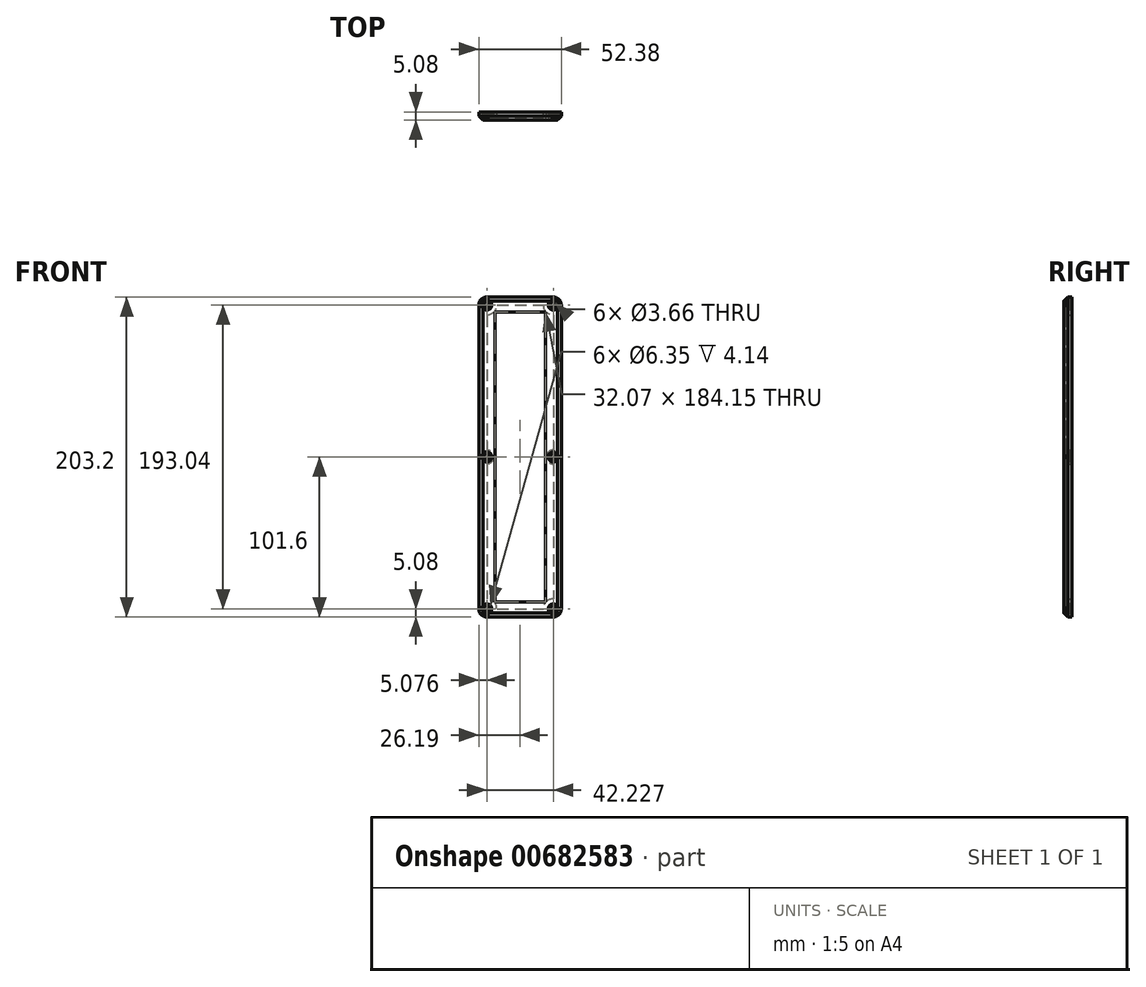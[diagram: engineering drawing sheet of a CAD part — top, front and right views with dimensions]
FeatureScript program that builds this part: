
annotation { "Feature Type Name" : "Feature", "Feature Type Description" : "" }
export const myFeature = defineFeature(function(context is Context, id is Id, definition is map)
    precondition{}
    {
        {
            var Q0;
            Q0=qCreatedBy(makeId("Front.planeOp"),FACE);
            var sketch = newSketch(context, id + "F0", { "sketchPlane" : qUnion([Q0])});
            skLineSegment(sketch, "E0.bottom", {"start": v(21.11, 101.6) * mm, "end": v(-21.11, 101.6) * mm});
            skLineSegment(sketch, "E0.top", {"start": v(21.11, -101.6) * mm, "end": v(-21.11, -101.6) * mm});
            skLineSegment(sketch, "E0.left", {"start": v(26.2, 96.52) * mm, "end": v(26.2, -96.52) * mm});
            skLineSegment(sketch, "E0.right", {"start": v(-26.2, 96.52) * mm, "end": v(-26.2, -96.52) * mm});
            skPoint(sketch, "E0.middle", {"position": v(0, 0) * mm});
            skPoint(sketch, "E1.visualSharp", {"position": v(-26.2, 101.6) * mm});
            skArc(sketch, "E1.filletArc", {"start": v(-21.11, 101.6) * mm, "mid": v(-24.7, 100.11) * mm, "end": v(-26.2, 96.52) * mm});
            skPoint(sketch, "E2.visualSharp", {"position": v(26.2, 101.6) * mm});
            skArc(sketch, "E2.filletArc", {"start": v(26.2, 96.52) * mm, "mid": v(24.7, 100.11) * mm, "end": v(21.11, 101.6) * mm});
            skPoint(sketch, "E3.visualSharp", {"position": v(-26.2, -101.6) * mm});
            skArc(sketch, "E3.filletArc", {"start": v(-26.2, -96.52) * mm, "mid": v(-24.7, -100.11) * mm, "end": v(-21.11, -101.6) * mm});
            skPoint(sketch, "E4.visualSharp", {"position": v(26.2, -101.6) * mm});
            skArc(sketch, "E4.filletArc", {"start": v(21.11, -101.6) * mm, "mid": v(24.7, -100.11) * mm, "end": v(26.2, -96.52) * mm});
            skSolve(sketch);
        }
        {
            var Q0;
            Q0=makeQuery(id+"F0.imprint","IMPRINT",FACE,{"disambiguationData":[TD([[makeQuery(id+"F0.imprint","IMPRINT",EDGE,{"derivedFrom":sQuery(id+"F0.wireOp",EDGE,"E0.bottom")}),1.0]])]});
            extrude(context, id + "F1", {"entities" : qUnion([Q0]), "depth" : 5.08 * mm, "offsetDistance" : 25.4 * mm});
        }
        {
            var Q0;
            Q0=makeQuery(id+"F1.opExtrude","CAP_EDGE",EDGE,{"disambiguationData":[OSD([sQuery(id+"F0.wireOp",EDGE,"E0.bottom")])],"isStart":false});
            chamfer(context, id + "F2", {"entities" : qUnion([Q0]), "width" : 2.54 * mm, "tangentPropagation" : true});
        }
        {
            var Q0;
            Q0=makeQuery(id+"F1.opExtrude","CAP_FACE",FACE,{"disambiguationData":[OSD([sQuery(id+"F0.wireOp",EDGE,"E0.bottom"),sQuery(id+"F0.wireOp",EDGE,"E0.top"),sQuery(id+"F0.wireOp",EDGE,"E0.left"),sQuery(id+"F0.wireOp",EDGE,"E0.right"),sQuery(id+"F0.wireOp",EDGE,"E1.filletArc"),sQuery(id+"F0.wireOp",EDGE,"E2.filletArc"),sQuery(id+"F0.wireOp",EDGE,"E3.filletArc"),sQuery(id+"F0.wireOp",EDGE,"E4.filletArc")])],"isStart":false});
            var sketch = newSketch(context, id + "F3", { "sketchPlane" : qUnion([Q0])});
            skPoint(sketch, "E5", {"position": v(-21.11, 96.52) * mm});
            skPoint(sketch, "E6", {"position": v(21.11, 96.52) * mm});
            skPoint(sketch, "E7", {"position": v(-21.11, -96.52) * mm});
            skPoint(sketch, "E8", {"position": v(21.11, -96.52) * mm});
            skPoint(sketch, "E9", {"position": v(-21.11, 0) * mm});
            skPoint(sketch, "E10", {"position": v(21.11, 0) * mm});
            skSolve(sketch);
        }
        {
            var Q0;
            Q0=sQuery(id+"F3.wireOp",VERTEX,"E5");
            var Q1;
            Q1=sQuery(id+"F3.wireOp",VERTEX,"E6");
            var Q2;
            Q2=sQuery(id+"F3.wireOp",VERTEX,"E10");
            var Q3;
            Q3=sQuery(id+"F3.wireOp",VERTEX,"E9");
            var Q4;
            Q4=sQuery(id+"F3.wireOp",VERTEX,"E7");
            var Q5;
            Q5=sQuery(id+"F3.wireOp",VERTEX,"E8");
            var Q6;
            Q6=makeQuery(id+"F1.opExtrude","SWEPT_BODY",BODY,{"disambiguationData":[OSD([sQuery(id+"F0.wireOp",EDGE,"E0.bottom"),sQuery(id+"F0.wireOp",EDGE,"E0.top"),sQuery(id+"F0.wireOp",EDGE,"E0.left"),sQuery(id+"F0.wireOp",EDGE,"E0.right"),sQuery(id+"F0.wireOp",EDGE,"E1.filletArc"),sQuery(id+"F0.wireOp",EDGE,"E2.filletArc"),sQuery(id+"F0.wireOp",EDGE,"E3.filletArc"),sQuery(id+"F0.wireOp",EDGE,"E4.filletArc")])]});
            hole(context, id + "F4", {"style" : HoleStyle.C_BORE, "endStyle" : HoleEndStyle.THROUGH, "holeDiameter" : 3.66 * mm, "cBoreDiameter" : 6.35 * mm, "cBoreDepth" : 3.5 * mm, "majorDiameter" : 6.35 * mm, "isTappedThrough" : true, "tappedDepth" : 12.7 * mm, "tapClearance" : 3, "locations" : qUnion([Q0, Q1, Q2, Q3, Q4, Q5]), "scope" : qUnion([Q6])});
        }
        {
            var Q0;
            Q0=makeQuery(id+"F1.opExtrude","CAP_FACE",FACE,{"disambiguationData":[OSD([sQuery(id+"F0.wireOp",EDGE,"E0.bottom"),sQuery(id+"F0.wireOp",EDGE,"E0.top"),sQuery(id+"F0.wireOp",EDGE,"E0.left"),sQuery(id+"F0.wireOp",EDGE,"E0.right"),sQuery(id+"F0.wireOp",EDGE,"E1.filletArc"),sQuery(id+"F0.wireOp",EDGE,"E2.filletArc"),sQuery(id+"F0.wireOp",EDGE,"E3.filletArc"),sQuery(id+"F0.wireOp",EDGE,"E4.filletArc")])],"isStart":false});
            var sketch = newSketch(context, id + "F5", { "sketchPlane" : qUnion([Q0])});
            skLineSegment(sketch, "E11.bottom", {"start": v(16.03, 92.08) * mm, "end": v(-16.03, 92.08) * mm});
            skLineSegment(sketch, "E11.top", {"start": v(16.03, -92.08) * mm, "end": v(-16.03, -92.08) * mm});
            skLineSegment(sketch, "E11.left", {"start": v(16.03, 92.08) * mm, "end": v(16.03, -92.08) * mm});
            skLineSegment(sketch, "E11.right", {"start": v(-16.03, 92.08) * mm, "end": v(-16.03, -92.08) * mm});
            skPoint(sketch, "E11.middle", {"position": v(0, 0) * mm});
            skSolve(sketch);
        }
        {
            var Q0;
            Q0=makeQuery(id+"F5.imprint","IMPRINT",FACE,{"disambiguationData":[TD([[makeQuery(id+"F5.imprint","IMPRINT",EDGE,{"derivedFrom":sQuery(id+"F5.wireOp",EDGE,"E11.bottom")}),1.0]])]});
            extrude(context, id + "F6", {"entities" : qUnion([Q0]), "operationType" : NewBodyOperationType.REMOVE, "endBound" : BoundingType.THROUGH_ALL, "oppositeDirection" : true, "depth" : 25.4 * mm, "offsetDistance" : 25.4 * mm});
        }
        {
            var Q0;
            Q0=makeQuery(id+"F1.opExtrude","CAP_FACE",FACE,{"disambiguationData":[OSD([sQuery(id+"F0.wireOp",EDGE,"E0.bottom"),sQuery(id+"F0.wireOp",EDGE,"E0.top"),sQuery(id+"F0.wireOp",EDGE,"E0.left"),sQuery(id+"F0.wireOp",EDGE,"E0.right"),sQuery(id+"F0.wireOp",EDGE,"E1.filletArc"),sQuery(id+"F0.wireOp",EDGE,"E2.filletArc"),sQuery(id+"F0.wireOp",EDGE,"E3.filletArc"),sQuery(id+"F0.wireOp",EDGE,"E4.filletArc")])],"isStart":true});
            var sketch = newSketch(context, id + "F7", { "sketchPlane" : qUnion([Q0])});
            skLineSegment(sketch, "E12.bottom", {"start": v(14.76, 96.52) * mm, "end": v(-14.76, 96.52) * mm});
            skLineSegment(sketch, "E12.top", {"start": v(14.76, -96.52) * mm, "end": v(-14.76, -96.52) * mm});
            skLineSegment(sketch, "E12.left", {"start": v(21.11, 90.17) * mm, "end": v(21.11, 4.45) * mm});
            skLineSegment(sketch, "E12.right", {"start": v(-21.11, 90.17) * mm, "end": v(-21.11, 4.45) * mm});
            skPoint(sketch, "E12.middle", {"position": v(0, 0) * mm});
            skArc(sketch, "E13", {"start": v(-21.11, 90.17) * mm, "mid": v(-16.62, 92.03) * mm, "end": v(-14.76, 96.52) * mm});
            skArc(sketch, "E14", {"start": v(14.76, 96.52) * mm, "mid": v(16.62, 92.03) * mm, "end": v(21.11, 90.17) * mm});
            skArc(sketch, "E15", {"start": v(-14.76, -96.52) * mm, "mid": v(-16.62, -92.03) * mm, "end": v(-21.11, -90.17) * mm});
            skArc(sketch, "E16", {"start": v(21.11, -90.17) * mm, "mid": v(16.62, -92.03) * mm, "end": v(14.76, -96.52) * mm});
            skArc(sketch, "E17", {"start": v(-21.11, -4.45) * mm, "mid": v(-16.67, 0) * mm, "end": v(-21.11, 4.45) * mm});
            skArc(sketch, "E18", {"start": v(21.11, 4.45) * mm, "mid": v(16.67, 0) * mm, "end": v(21.11, -4.45) * mm});
            skLineSegment(sketch, "E19.trimOffspring", {"start": v(-21.11, -4.45) * mm, "end": v(-21.11, -90.17) * mm});
            skLineSegment(sketch, "E20.trimOffspring", {"start": v(21.11, -4.45) * mm, "end": v(21.11, -90.17) * mm});
            skSolve(sketch);
        }
        {
            var Q0;
            Q0=makeQuery(id+"F7.imprint","IMPRINT",FACE,{"disambiguationData":[TD([[makeQuery(id+"F7.imprint","IMPRINT",EDGE,{"derivedFrom":sQuery(id+"F7.wireOp",EDGE,"E12.bottom")}),1.0]])]});
            extrude(context, id + "F8", {"entities" : qUnion([Q0]), "operationType" : NewBodyOperationType.REMOVE, "oppositeDirection" : true, "depth" : 3.28 * mm, "offsetDistance" : 25.4 * mm});
        }
    });
